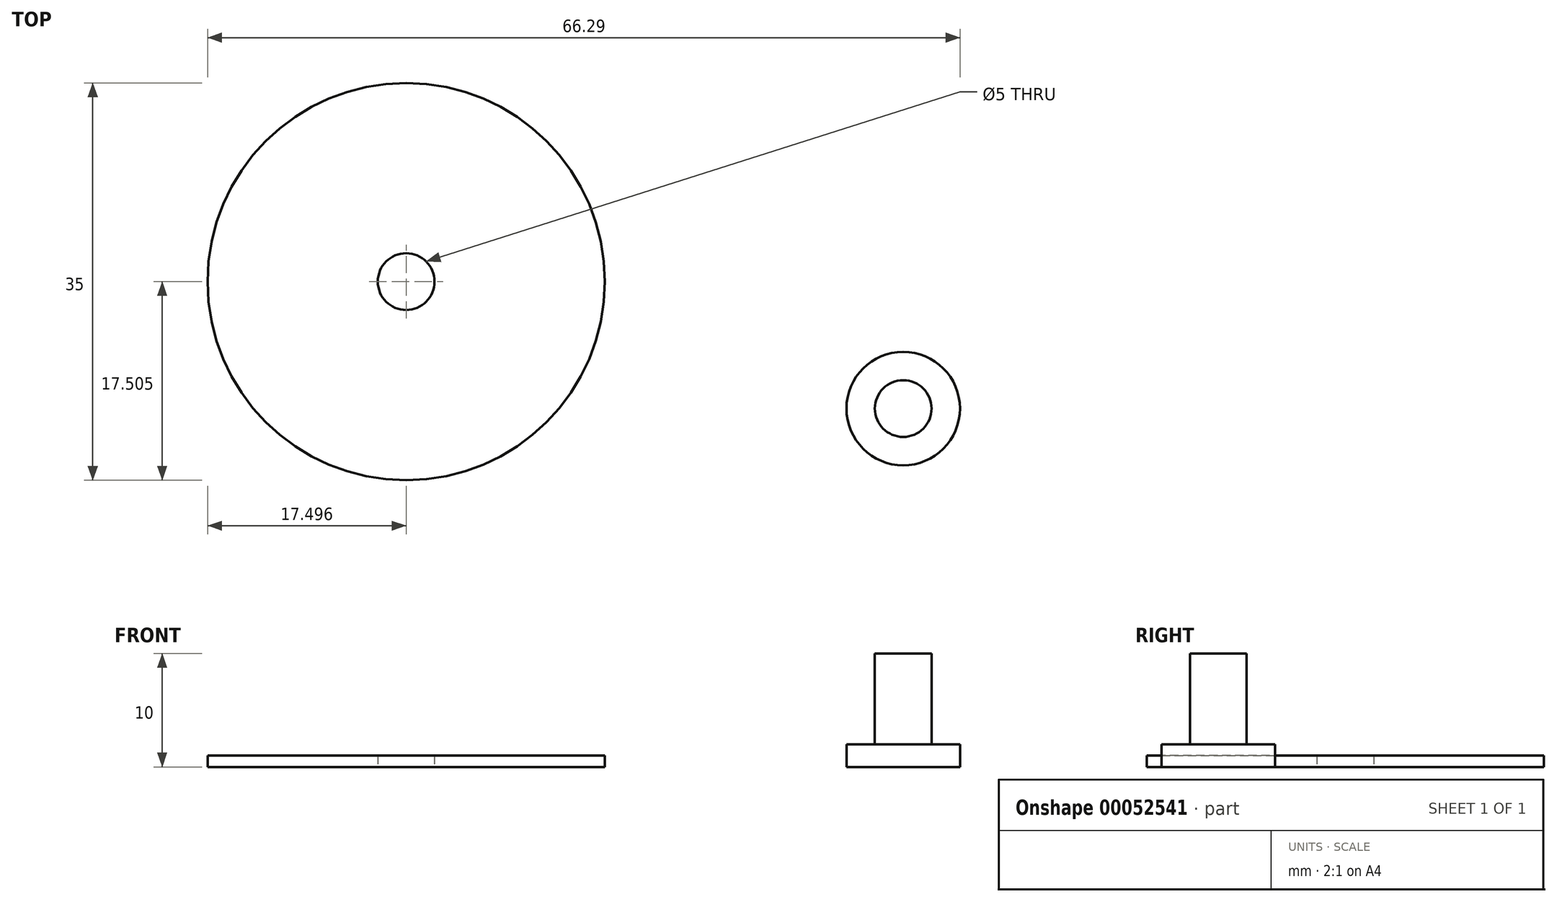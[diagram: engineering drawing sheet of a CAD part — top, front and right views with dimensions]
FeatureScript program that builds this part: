
annotation { "Feature Type Name" : "Feature", "Feature Type Description" : "" }
export const myFeature = defineFeature(function(context is Context, id is Id, definition is map)
    precondition{}
    {
        {
            var Q0;
            Q0=qCreatedBy(makeId("Top.planeOp"),FACE);
            var sketch = newSketch(context, id + "F0", { "sketchPlane" : qUnion([Q0])});
            skCircle(sketch, "E0", {"center": v(0, 0) * mm, "radius": 5 * mm});
            skCircle(sketch, "E1", {"center": v(0, 0) * mm, "radius": 2.5 * mm});
            skSolve(sketch);
        }
        {
            var Q0;
            Q0 = qSketchRegion(id + "F0", true);
            extrude(context, id + "F1", {"entities" : qUnion([Q0]), "depth" : 2 * mm});
        }
        {
            var Q0;
            Q0=qCreatedBy(makeId("Top.planeOp"),FACE);
            var sketch = newSketch(context, id + "F2", { "sketchPlane" : qUnion([Q0])});
            skCircle(sketch, "E2", {"center": v(-43.8, 11.18) * mm, "radius": 17.5 * mm});
            skCircle(sketch, "E3", {"center": v(-43.8, 11.18) * mm, "radius": 2.5 * mm});
            skSolve(sketch);
        }
        {
            var Q0;
            Q0=makeQuery(id+"F2.imprint","IMPRINT",FACE,{"disambiguationData":[TD([[makeQuery(id+"F2.imprint","IMPRINT",EDGE,{"derivedFrom":sQuery(id+"F2.wireOp",EDGE,"E2")}),1.0]])]});
            extrude(context, id + "F3", {"entities" : qUnion([Q0]), "depth" : 1 * mm});
        }
        {
            var Q0;
            Q0=qCreatedBy(makeId("Top.planeOp"),FACE);
            var sketch = newSketch(context, id + "F4", { "sketchPlane" : qUnion([Q0])});
            skCircle(sketch, "E4", {"center": v(0, 0) * mm, "radius": 2.5 * mm});
            skSolve(sketch);
        }
        {
            var Q0;
            Q0=makeQuery(id+"F4.imprint","IMPRINT",FACE,{"disambiguationData":[TD([[makeQuery(id+"F4.imprint","IMPRINT",EDGE,{"derivedFrom":sQuery(id+"F4.wireOp",EDGE,"E4")}),1.0]])]});
            extrude(context, id + "F5", {"entities" : qUnion([Q0]), "operationType" : NewBodyOperationType.ADD, "depth" : 10 * mm});
        }
    });
